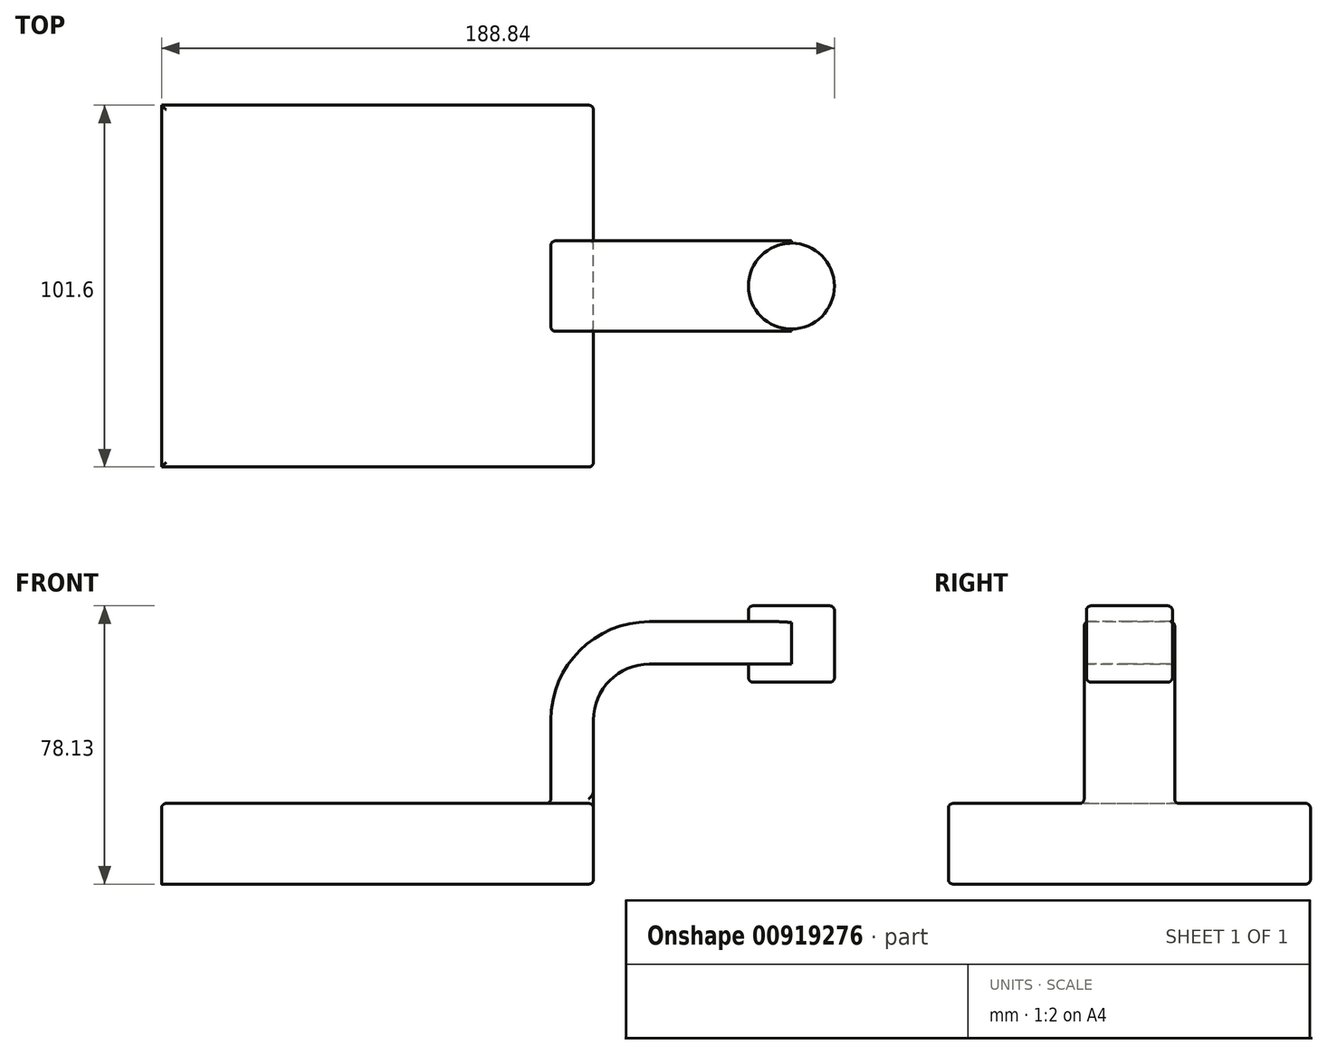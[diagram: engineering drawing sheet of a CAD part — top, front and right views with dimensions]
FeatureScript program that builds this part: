
annotation { "Feature Type Name" : "Feature", "Feature Type Description" : "" }
export const myFeature = defineFeature(function(context is Context, id is Id, definition is map)
    precondition{}
    {
        {
            var Q0;
            Q0=qCreatedBy(makeId("Front.planeOp"),FACE);
            var sketch = newSketch(context, id + "F0", { "sketchPlane" : qUnion([Q0])});
            skLineSegment(sketch, "E0.bottom", {"start": v(-60.58, 26.3) * mm, "end": v(60.62, 26.3) * mm});
            skLineSegment(sketch, "E0.top", {"start": v(-60.58, 3.65) * mm, "end": v(60.62, 3.65) * mm});
            skLineSegment(sketch, "E0.left", {"start": v(-60.58, 26.3) * mm, "end": v(-60.58, 3.65) * mm});
            skLineSegment(sketch, "E0.right", {"start": v(60.62, 26.3) * mm, "end": v(60.62, 3.65) * mm});
            skLineSegment(sketch, "E1.bottom", {"start": v(79.96, 60.36) * mm, "end": v(128.26, 60.36) * mm});
            skLineSegment(sketch, "E1.top", {"start": v(79.96, 81.78) * mm, "end": v(128.26, 81.78) * mm});
            skLineSegment(sketch, "E1.left", {"start": v(79.96, 60.36) * mm, "end": v(79.96, 81.78) * mm});
            skLineSegment(sketch, "E1.right", {"start": v(128.26, 60.36) * mm, "end": v(128.26, 81.78) * mm});
            skLineSegment(sketch, "E2", {"start": v(60.62, 26.3) * mm, "end": v(60.62, 49.73) * mm});
            skArc(sketch, "E3", {"start": v(60.62, 49.73) * mm, "mid": v(65.21, 60.81) * mm, "end": v(76.3, 65.4) * mm});
            skLineSegment(sketch, "E4", {"start": v(76.3, 65.4) * mm, "end": v(116.2, 65.4) * mm});
            skLineSegment(sketch, "E5.0", {"start": v(76.3, 77.34) * mm, "end": v(116.2, 77.34) * mm});
            skArc(sketch, "E5.1", {"start": v(48.68, 49.73) * mm, "mid": v(56.77, 69.25) * mm, "end": v(76.3, 77.34) * mm});
            skLineSegment(sketch, "E5.2", {"start": v(48.68, 26.3) * mm, "end": v(48.68, 49.73) * mm});
            skLineSegment(sketch, "E6", {"start": v(116.2, 65.4) * mm, "end": v(116.2, 81.78) * mm});
            skLineSegment(sketch, "E7", {"start": v(116.2, 65.4) * mm, "end": v(116.2, 60.36) * mm});
            skFitSpline(sketch, "E8", {"points": [v(-60.58, 26.3) * mm, v(76.3, 77.34) * mm], "startDerivative": vector(270.57, 16.42) * mm, "endDerivative": vector(163.95, -1.87) * mm});
            skSolve(sketch);
        }
        {
            var Q0;
            Q0=makeQuery(id+"F0.imprint","IMPRINT",FACE,{"disambiguationData":[TD([[makeQuery(id+"F0.imprint","IMPRINT",EDGE,{"derivedFrom":sQuery(id+"F0.wireOp",EDGE,"E0.top")}),1.0]])]});
            extrude(context, id + "F1", {"entities" : qUnion([Q0]), "endBound" : BoundingType.SYMMETRIC, "depth" : 101.6 * mm, "offsetDistance" : 25.4 * mm});
        }
        {
            var Q0;
            {var subQ1=sQuery(id+"F0.wireOp",EDGE,"E2");Q0=makeQuery(id+"F0.imprint","IMPRINT",FACE,{"disambiguationData":[TD([[makeQuery(id+"F0.imprint","IMPRINT",EDGE,{"derivedFrom":subQ1}),1.0]])]});}
            var Q1;
            {var subQ0=sQuery(id+"F0.wireOp",EDGE,"E4");var subQ1=sQuery(id+"F0.wireOp",EDGE,"E1.left");var subQ2=makeQuery(id+"F0.imprint","INTERSECT",VERTEX,{"derivedFrom":[subQ1,subQ0]});Q1=makeQuery(id+"F0.imprint","IMPRINT",FACE,{"disambiguationData":[TD([[makeQuery(id+"F0.imprint","IMPRINT",EDGE,{"disambiguationData":[TD([[subQ2,-1.0]])],"derivedFrom":subQ1}),-1.0]])]});}
            extrude(context, id + "F2", {"entities" : qUnion([Q0, Q1]), "operationType" : NewBodyOperationType.ADD, "endBound" : BoundingType.SYMMETRIC, "depth" : 25.4 * mm, "offsetDistance" : 25.4 * mm});
        }
        {
            var Q0;
            Q0=makeQuery(id+"F0.imprint","IMPRINT",FACE,{"disambiguationData":[TD([[makeQuery(id+"F0.imprint","IMPRINT",EDGE,{"derivedFrom":sQuery(id+"F0.wireOp",EDGE,"E5.1")}),1.0]])]});
            extrude(context, id + "F3", {"entities" : qUnion([Q0]), "operationType" : NewBodyOperationType.ADD, "endBound" : BoundingType.SYMMETRIC, "depth" : 15.24 * mm, "offsetDistance" : 25.4 * mm});
        }
        {
            var Q0;
            {var subQ0=sQuery(id+"F0.wireOp",EDGE,"E1.right");Q0=makeQuery(id+"F0.imprint","IMPRINT",FACE,{"disambiguationData":[TD([[makeQuery(id+"F0.imprint","IMPRINT",EDGE,{"derivedFrom":subQ0}),1.0]])]});}
            var Q1;
            Q1=sQuery(id+"F0.wireOp",EDGE,"E6");
            revolve(context, id + "F4", {"operationType" : NewBodyOperationType.ADD, "surfaceOperationType" : NewSurfaceOperationType.NEW, "entities" : qUnion([Q0]), "axis" : qUnion([Q1]), "revolveType" : RevolveType.FULL});
        }
        {
            var Q0;
            Q0=makeQuery(id+"F1.opExtrude","CAP_EDGE",EDGE,{"disambiguationData":[OSD([sQuery(id+"F0.wireOp",EDGE,"E0.bottom")])],"isStart":false});
            var Q1;
            {var subQ0=sQuery(id+"F0.wireOp",EDGE,"E2");var subQ1=sQuery(id+"F0.wireOp",EDGE,"E0.bottom");var subQ2=sQuery(id+"F0.wireOp",EDGE,"E0.right");Q1=makeQuery(id+"F2.boolean.opBoolean","SPLIT",EDGE,{"disambiguationData":[TD([makeQuery(id+"F1.opExtrude","CAP_FACE",FACE,{"disambiguationData":[OSD([subQ1,sQuery(id+"F0.wireOp",EDGE,"E0.top"),sQuery(id+"F0.wireOp",EDGE,"E0.left"),subQ2])],"isStart":false})])],"derivedFrom":makeQuery(id+"F1.opExtrude","SWEPT_EDGE",EDGE,{"disambiguationData":[OSD([subQ1,subQ2,subQ0])]})});}
            var Q2;
            Q2=makeQuery(id+"F2.opExtrude","CAP_EDGE",EDGE,{"disambiguationData":[OSD([sQuery(id+"F0.wireOp",EDGE,"E0.bottom")])],"isStart":false});
            var Q3;
            Q3=makeQuery(id+"F2.opExtrude","CAP_EDGE",EDGE,{"disambiguationData":[OSD([sQuery(id+"F0.wireOp",EDGE,"E5.1")])],"isStart":false});
            var Q4;
            Q4=makeQuery(id+"F3.opExtrude","CAP_EDGE",EDGE,{"disambiguationData":[OSD([sQuery(id+"F0.wireOp",EDGE,"E8")])],"isStart":true});
            var Q5;
            Q5=makeQuery(id+"F2.opExtrude","CAP_EDGE",EDGE,{"disambiguationData":[OSD([sQuery(id+"F0.wireOp",EDGE,"E5.1")])],"isStart":true});
            var Q6;
            Q6=makeQuery(id+"F2.opExtrude","CAP_EDGE",EDGE,{"disambiguationData":[OSD([sQuery(id+"F0.wireOp",EDGE,"E2")])],"isStart":true});
            var Q7;
            Q7=makeQuery(id+"F4.opRevolve","SWEPT_EDGE",EDGE,{"disambiguationData":[OSD([sQuery(id+"F0.wireOp",EDGE,"E1.top"),sQuery(id+"F0.wireOp",EDGE,"E1.right")])]});
            var Q8;
            Q8=makeQuery(id+"F4.opRevolve","SWEPT_EDGE",EDGE,{"disambiguationData":[OSD([sQuery(id+"F0.wireOp",EDGE,"E1.bottom"),sQuery(id+"F0.wireOp",EDGE,"E1.right")])]});
            var Q9;
            {var subQ0=sQuery(id+"F0.wireOp",EDGE,"E2");var subQ1=sQuery(id+"F0.wireOp",EDGE,"E0.bottom");var subQ2=sQuery(id+"F0.wireOp",EDGE,"E0.right");Q9=makeQuery(id+"F2.boolean.opBoolean","SPLIT",EDGE,{"disambiguationData":[TD([makeQuery(id+"F1.opExtrude","CAP_FACE",FACE,{"disambiguationData":[OSD([subQ1,sQuery(id+"F0.wireOp",EDGE,"E0.top"),sQuery(id+"F0.wireOp",EDGE,"E0.left"),subQ2])],"isStart":true})])],"derivedFrom":makeQuery(id+"F1.opExtrude","SWEPT_EDGE",EDGE,{"disambiguationData":[OSD([subQ1,subQ2,subQ0])]})});}
            var Q10;
            {var subQ3=sQuery(id+"F0.wireOp",EDGE,"E0.bottom");var subQ4=sQuery(id+"F0.wireOp",EDGE,"E0.right");var subQ5=sQuery(id+"F0.wireOp",EDGE,"E0.left");Q10=makeQuery(id+"F3.boolean.opBoolean","SPLIT",FACE,{"disambiguationData":[TD([makeQuery(id+"F1.opExtrude","CAP_FACE",FACE,{"disambiguationData":[OSD([subQ3,sQuery(id+"F0.wireOp",EDGE,"E0.top"),subQ5,subQ4])],"isStart":true})])],"derivedFrom":makeQuery(id+"F1.opExtrude","SWEPT_FACE",FACE,{"disambiguationData":[OSD([subQ3])]})});}
            var Q11;
            Q11=makeQuery(id+"F3.opExtrude","CAP_EDGE",EDGE,{"disambiguationData":[OSD([sQuery(id+"F0.wireOp",EDGE,"E8")])],"isStart":false});
            var Q12;
            {var subQ3=sQuery(id+"F0.wireOp",EDGE,"E0.bottom");var subQ5=sQuery(id+"F0.wireOp",EDGE,"E0.right");var subQ6=sQuery(id+"F0.wireOp",EDGE,"E0.left");Q12=makeQuery(id+"F3.boolean.opBoolean","SPLIT",FACE,{"disambiguationData":[TD([makeQuery(id+"F1.opExtrude","CAP_FACE",FACE,{"disambiguationData":[OSD([subQ3,sQuery(id+"F0.wireOp",EDGE,"E0.top"),subQ6,subQ5])],"isStart":false})])],"derivedFrom":makeQuery(id+"F1.opExtrude","SWEPT_FACE",FACE,{"disambiguationData":[OSD([subQ3])]})});}
            var Q13;
            Q13=makeQuery(id+"F1.opExtrude","CAP_EDGE",EDGE,{"disambiguationData":[OSD([sQuery(id+"F0.wireOp",EDGE,"E0.top")])],"isStart":true});
            var Q14;
            Q14=makeQuery(id+"F1.opExtrude","CAP_EDGE",EDGE,{"disambiguationData":[OSD([sQuery(id+"F0.wireOp",EDGE,"E0.right")])],"isStart":true});
            var Q15;
            Q15=makeQuery(id+"F1.opExtrude","CAP_EDGE",EDGE,{"disambiguationData":[OSD([sQuery(id+"F0.wireOp",EDGE,"E0.right")])],"isStart":false});
            var Q16;
            Q16=makeQuery(id+"F1.opExtrude","SWEPT_EDGE",EDGE,{"disambiguationData":[OSD([sQuery(id+"F0.wireOp",EDGE,"E0.top"),sQuery(id+"F0.wireOp",EDGE,"E0.right")])]});
            var Q17;
            Q17=makeQuery(id+"F1.opExtrude","CAP_EDGE",EDGE,{"disambiguationData":[OSD([sQuery(id+"F0.wireOp",EDGE,"E0.top")])],"isStart":false});
            fillet(context, id + "F5", {"entities" : qUnion([Q0, Q1, Q2, Q3, Q4, Q5, Q6, Q7, Q8, Q9, Q10, Q11, Q12, Q13, Q14, Q15, Q16, Q17]), "radius" : 1.27 * mm, "tangentPropagation" : true, "allowEdgeOverflow" : false});
        }
    });
